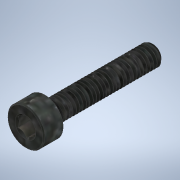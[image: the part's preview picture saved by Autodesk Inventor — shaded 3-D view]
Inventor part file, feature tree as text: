
AUTODESK INVENTOR PART (.ipt)
format: ipt  version: 2020.5 (Build 245400000, 400)  size: 804,352 bytes
history: native  units: in
note: dims shown in document units (in); Inventor stores cm internally (conversion verified against a paired STEP export)
features: revolve x1
ambient origin geometry x8: Origin, YZ Plane, XZ Plane, XY Plane, X Axis, Y Axis, Z Axis, Center Point
bodies: Solid1 (feature_tree)
feature tree (1):
  revolve  "Revolve2"  [1 undecoded]
note: 1 required parameter value undecoded (feature->parameter linkage not recoverable at this tier; creation-order binding heuristic only, values carry confidence <= 0.55)
